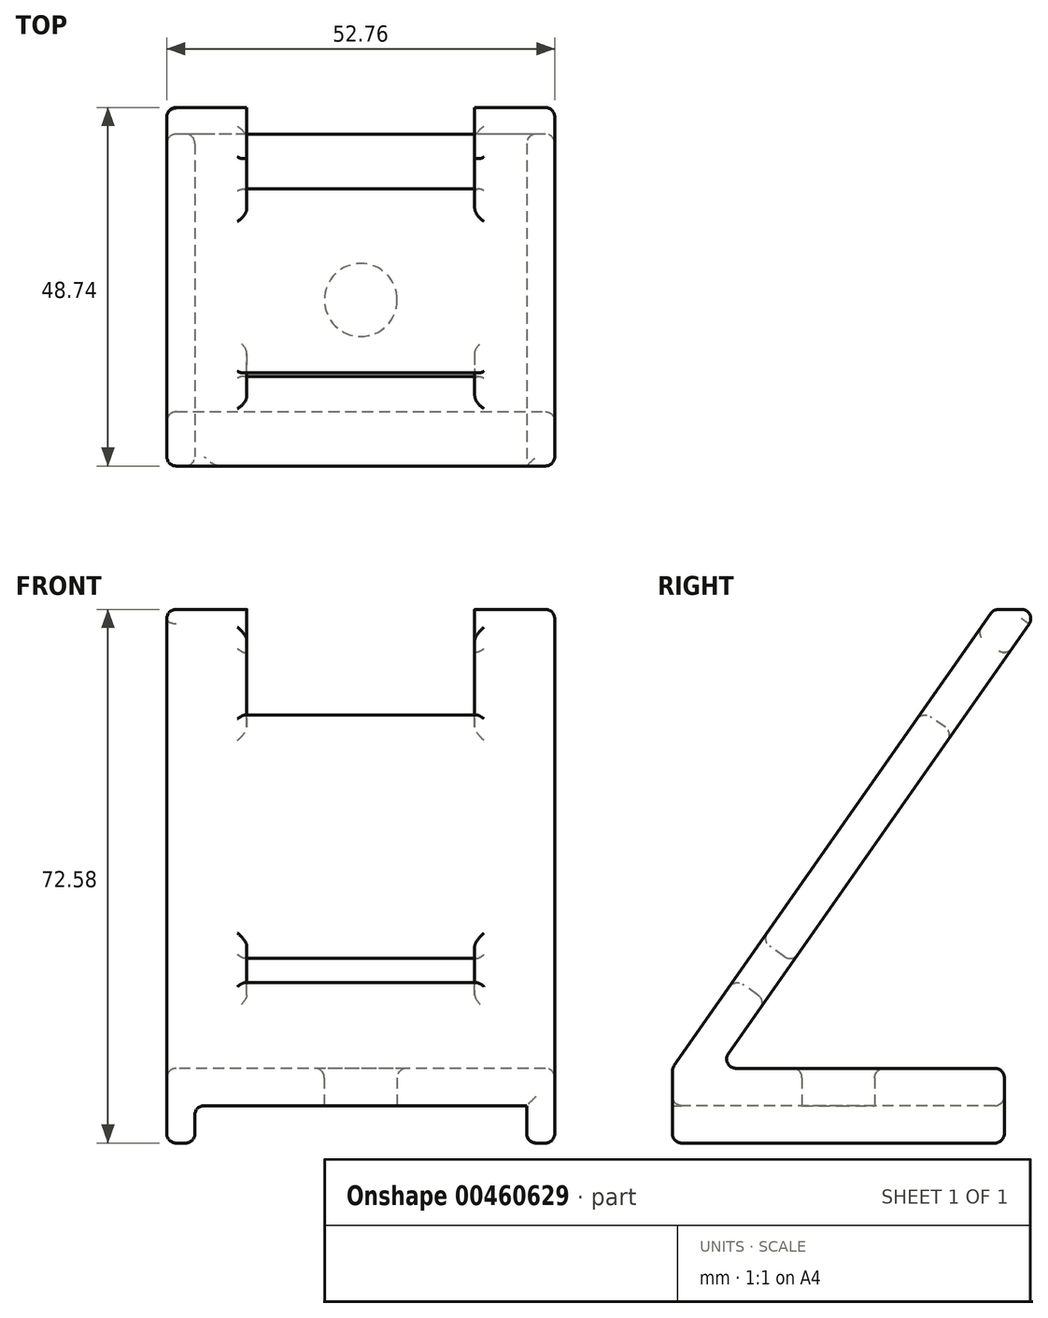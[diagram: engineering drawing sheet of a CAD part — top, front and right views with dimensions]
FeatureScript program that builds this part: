
annotation { "Feature Type Name" : "Feature", "Feature Type Description" : "" }
export const myFeature = defineFeature(function(context is Context, id is Id, definition is map)
    precondition{}
    {
        {
            var Q0;
            Q0=qCreatedBy(makeId("Top.planeOp"),FACE);
            var sketch = newSketch(context, id + "F0", { "sketchPlane" : qUnion([Q0])});
            skLineSegment(sketch, "E0.bottom", {"start": v(26.38, -22.57) * mm, "end": v(-26.38, -22.57) * mm});
            skLineSegment(sketch, "E0.top", {"start": v(26.38, 22.57) * mm, "end": v(-26.38, 22.57) * mm});
            skLineSegment(sketch, "E0.left", {"start": v(26.38, -22.57) * mm, "end": v(26.38, 22.57) * mm});
            skLineSegment(sketch, "E0.right", {"start": v(-26.38, -22.57) * mm, "end": v(-26.38, 22.57) * mm});
            skPoint(sketch, "E0.middle", {"position": v(0, 0) * mm});
            skSolve(sketch);
        }
        {
            var Q0;
            Q0=makeQuery(id+"F0.imprint","IMPRINT",FACE,{"disambiguationData":[TD([[makeQuery(id+"F0.imprint","IMPRINT",EDGE,{"derivedFrom":sQuery(id+"F0.wireOp",EDGE,"E0.bottom")}),-1.0]])]});
            extrude(context, id + "F1", {"entities" : qUnion([Q0]), "depth" : 5.08 * mm});
        }
        {
            var Q0;
            Q0=qCreatedBy(makeId("Top.planeOp"),FACE);
            var sketch = newSketch(context, id + "F2", { "sketchPlane" : qUnion([Q0])});
            skLineSegment(sketch, "E1.0", {"start": v(26.38, -22.57) * mm, "end": v(26.38, 22.57) * mm});
            skLineSegment(sketch, "E2.0", {"start": v(26.38, 22.57) * mm, "end": v(22.57, 22.57) * mm});
            skLineSegment(sketch, "E3.0", {"start": v(-26.38, -22.57) * mm, "end": v(-26.38, 22.57) * mm});
            skLineSegment(sketch, "E4.0", {"start": v(26.38, -22.57) * mm, "end": v(22.57, -22.57) * mm});
            skLineSegment(sketch, "E5", {"start": v(22.57, 22.57) * mm, "end": v(22.57, -22.57) * mm});
            skLineSegment(sketch, "E6", {"start": v(-22.57, 22.57) * mm, "end": v(-22.57, -22.57) * mm});
            skLineSegment(sketch, "E7.trimOffspring", {"start": v(-22.57, 22.57) * mm, "end": v(-26.38, 22.57) * mm});
            skLineSegment(sketch, "E8.trimOffspring", {"start": v(-22.57, -22.57) * mm, "end": v(-26.38, -22.57) * mm});
            skSolve(sketch);
        }
        {
            var Q0;
            Q0=makeQuery(id+"F2.imprint","IMPRINT",FACE,{"disambiguationData":[TD([[makeQuery(id+"F2.imprint","IMPRINT",EDGE,{"derivedFrom":sQuery(id+"F2.wireOp",EDGE,"E1.0")}),1.0]])]});
            var Q1;
            Q1=makeQuery(id+"F2.imprint","IMPRINT",FACE,{"disambiguationData":[TD([[makeQuery(id+"F2.imprint","IMPRINT",EDGE,{"derivedFrom":sQuery(id+"F2.wireOp",EDGE,"E3.0")}),-1.0]])]});
            extrude(context, id + "F3", {"entities" : qUnion([Q0, Q1]), "operationType" : NewBodyOperationType.ADD, "oppositeDirection" : true, "depth" : 5.08 * mm});
        }
        {
            var Q0;
            Q0=qCreatedBy(makeId("Top.planeOp"),FACE);
            var sketch = newSketch(context, id + "F4", { "sketchPlane" : qUnion([Q0])});
            skCircle(sketch, "E9", {"center": v(0, 0) * mm, "radius": 4.95 * mm});
            skSolve(sketch);
        }
        {
            var Q0;
            Q0=makeQuery(id+"F4.imprint","IMPRINT",FACE,{"disambiguationData":[TD([[makeQuery(id+"F4.imprint","IMPRINT",EDGE,{"derivedFrom":sQuery(id+"F4.wireOp",EDGE,"E9")}),1.0]])]});
            extrude(context, id + "F5", {"entities" : qUnion([Q0]), "operationType" : NewBodyOperationType.REMOVE, "depth" : 25.4 * mm});
        }
        {
            var Q0;
            Q0=qCreatedBy(makeId("Right.planeOp"),FACE);
            var sketch = newSketch(context, id + "F6", { "sketchPlane" : qUnion([Q0])});
            skLineSegment(sketch, "E10.0", {"start": v(-22.57, 5.08) * mm, "end": v(22.57, 5.08) * mm});
            skLineSegment(sketch, "E11", {"start": v(-22.57, 5.08) * mm, "end": v(21.14, 67.5) * mm});
            skLineSegment(sketch, "E12", {"start": v(21.14, 67.5) * mm, "end": v(27.34, 67.5) * mm});
            skLineSegment(sketch, "E13", {"start": v(27.34, 67.5) * mm, "end": v(-16.37, 5.08) * mm});
            skSolve(sketch);
        }
        {
            var Q0;
            {var subQ0=sQuery(id+"F6.wireOp",EDGE,"E11");Q0=makeQuery(id+"F6.imprint","IMPRINT",FACE,{"disambiguationData":[TD([[makeQuery(id+"F6.imprint","IMPRINT",EDGE,{"derivedFrom":subQ0}),-1.0]])]});}
            extrude(context, id + "F7", {"entities" : qUnion([Q0]), "operationType" : NewBodyOperationType.ADD, "endBound" : BoundingType.SYMMETRIC, "depth" : 52.76 * mm});
        }
        {
            var Q0;
            Q0=makeQuery(id+"F7.opExtrude","SWEPT_FACE",FACE,{"disambiguationData":[OSD([sQuery(id+"F6.wireOp",EDGE,"E11")])]});
            var sketch = newSketch(context, id + "F8", { "sketchPlane" : qUnion([Q0])});
            skLineSegment(sketch, "E14.bottom", {"start": v(15.5, 50.5) * mm, "end": v(-15.5, 50.5) * mm});
            skLineSegment(sketch, "E14.top", {"start": v(15.5, 63.2) * mm, "end": v(-15.5, 63.2) * mm});
            skLineSegment(sketch, "E14.left", {"start": v(15.5, 50.5) * mm, "end": v(15.5, 63.2) * mm});
            skLineSegment(sketch, "E14.right", {"start": v(-15.5, 50.5) * mm, "end": v(-15.5, 63.2) * mm});
            skPoint(sketch, "E14.middle", {"position": v(0, 56.85) * mm});
            skSolve(sketch);
        }
        {
            var Q0;
            Q0=makeQuery(id+"F8.imprint","IMPRINT",FACE,{"disambiguationData":[TD([[makeQuery(id+"F8.imprint","IMPRINT",EDGE,{"derivedFrom":sQuery(id+"F8.wireOp",EDGE,"E14.bottom")}),-1.0]])]});
            extrude(context, id + "F9", {"entities" : qUnion([Q0]), "operationType" : NewBodyOperationType.REMOVE, "endBound" : BoundingType.THROUGH_ALL, "oppositeDirection" : true, "depth" : 25.4 * mm});
        }
        {
            var Q0;
            Q0=makeQuery(id+"F7.opExtrude","SWEPT_FACE",FACE,{"disambiguationData":[OSD([sQuery(id+"F6.wireOp",EDGE,"E11")])]});
            var sketch = newSketch(context, id + "F10", { "sketchPlane" : qUnion([Q0])});
            skLineSegment(sketch, "E15", {"start": v(15.5, 12.4) * mm, "end": v(15.5, 6.05) * mm});
            skPoint(sketch, "E15.startSnap0", {"position": v(15.5, 56.85) * mm});
            skLineSegment(sketch, "E16", {"start": v(15.5, 6.05) * mm, "end": v(-15.5, 6.05) * mm});
            skLineSegment(sketch, "E17", {"start": v(-15.5, 6.05) * mm, "end": v(-15.5, 12.4) * mm});
            skLineSegment(sketch, "E18", {"start": v(-15.5, 12.4) * mm, "end": v(15.5, 12.4) * mm});
            skSolve(sketch);
        }
        {
            var Q0;
            Q0=makeQuery(id+"F10.imprint","IMPRINT",FACE,{"disambiguationData":[TD([[makeQuery(id+"F10.imprint","IMPRINT",EDGE,{"derivedFrom":sQuery(id+"F10.wireOp",EDGE,"E15")}),-1.0]])]});
            extrude(context, id + "F11", {"entities" : qUnion([Q0]), "operationType" : NewBodyOperationType.REMOVE, "endBound" : BoundingType.UP_TO_NEXT, "oppositeDirection" : true, "depth" : 25.4 * mm});
        }
        {
            var Q0;
            Q0=makeQuery(id+"F7.boolean.opBoolean","MERGE",FACE,{"derivedFrom":[makeQuery(id+"F3.boolean.opBoolean","MERGE",FACE,{"derivedFrom":[makeQuery(id+"F1.opExtrude","SWEPT_FACE",FACE,{"disambiguationData":[OSD([sQuery(id+"F0.wireOp",EDGE,"E0.left")])]}),makeQuery(id+"F3.opExtrude","SWEPT_FACE",FACE,{"disambiguationData":[OSD([sQuery(id+"F2.wireOp",EDGE,"E1.0")])]})]}),makeQuery(id+"F7.opExtrude","CAP_FACE",FACE,{"disambiguationData":[OSD([sQuery(id+"F6.wireOp",EDGE,"E10.0"),sQuery(id+"F6.wireOp",EDGE,"E11"),sQuery(id+"F6.wireOp",EDGE,"E12"),sQuery(id+"F6.wireOp",EDGE,"E13")])],"isStart":false})]});
            var Q1;
            Q1=makeQuery(id+"F7.boolean.opBoolean","MERGE",FACE,{"derivedFrom":[makeQuery(id+"F3.boolean.opBoolean","MERGE",FACE,{"derivedFrom":[makeQuery(id+"F1.opExtrude","SWEPT_FACE",FACE,{"disambiguationData":[OSD([sQuery(id+"F0.wireOp",EDGE,"E0.right")])]}),makeQuery(id+"F3.opExtrude","SWEPT_FACE",FACE,{"disambiguationData":[OSD([sQuery(id+"F2.wireOp",EDGE,"E3.0")])]})]}),makeQuery(id+"F7.opExtrude","CAP_FACE",FACE,{"disambiguationData":[OSD([sQuery(id+"F6.wireOp",EDGE,"E10.0"),sQuery(id+"F6.wireOp",EDGE,"E11"),sQuery(id+"F6.wireOp",EDGE,"E12"),sQuery(id+"F6.wireOp",EDGE,"E13")])],"isStart":true})]});
            var Q2;
            Q2=makeQuery(id+"F7.opExtrude","SWEPT_FACE",FACE,{"disambiguationData":[OSD([sQuery(id+"F6.wireOp",EDGE,"E11")])]});
            var Q3;
            Q3=makeQuery(id+"F7.opExtrude","SWEPT_FACE",FACE,{"disambiguationData":[OSD([sQuery(id+"F6.wireOp",EDGE,"E13")])]});
            var Q4;
            Q4=makeQuery(id+"F1.opExtrude","CAP_FACE",FACE,{"disambiguationData":[OSD([sQuery(id+"F0.wireOp",EDGE,"E0.bottom"),sQuery(id+"F0.wireOp",EDGE,"E0.top"),sQuery(id+"F0.wireOp",EDGE,"E0.left"),sQuery(id+"F0.wireOp",EDGE,"E0.right")])],"isStart":false});
            var Q5;
            Q5=makeQuery(id+"F3.boolean.opBoolean","MERGE",FACE,{"derivedFrom":[makeQuery(id+"F1.opExtrude","SWEPT_FACE",FACE,{"disambiguationData":[OSD([sQuery(id+"F0.wireOp",EDGE,"E0.top")])]}),makeQuery(id+"F3.opExtrude","SWEPT_FACE",FACE,{"disambiguationData":[OSD([sQuery(id+"F2.wireOp",EDGE,"E2.0")])]}),makeQuery(id+"F3.opExtrude","SWEPT_FACE",FACE,{"disambiguationData":[OSD([sQuery(id+"F2.wireOp",EDGE,"E7.trimOffspring")])]})]});
            var Q6;
            Q6=makeQuery(id+"F3.opExtrude","CAP_EDGE",EDGE,{"disambiguationData":[OSD([sQuery(id+"F2.wireOp",EDGE,"E5")])],"isStart":true});
            var Q7;
            Q7=makeQuery(id+"F3.opExtrude","SWEPT_FACE",FACE,{"disambiguationData":[OSD([sQuery(id+"F2.wireOp",EDGE,"E6")])]});
            var Q8;
            Q8=makeQuery(id+"F3.opExtrude","CAP_FACE",FACE,{"disambiguationData":[OSD([sQuery(id+"F2.wireOp",EDGE,"E1.0"),sQuery(id+"F2.wireOp",EDGE,"E2.0"),sQuery(id+"F2.wireOp",EDGE,"E4.0"),sQuery(id+"F2.wireOp",EDGE,"E5")])],"isStart":false});
            var Q9;
            Q9=makeQuery(id+"F3.opExtrude","CAP_FACE",FACE,{"disambiguationData":[OSD([sQuery(id+"F2.wireOp",EDGE,"E3.0"),sQuery(id+"F2.wireOp",EDGE,"E6"),sQuery(id+"F2.wireOp",EDGE,"E7.trimOffspring"),sQuery(id+"F2.wireOp",EDGE,"E8.trimOffspring")])],"isStart":false});
            fillet(context, id + "F12", {"entities" : qUnion([Q0, Q1, Q2, Q3, Q4, Q5, Q6, Q7, Q8, Q9]), "radius" : 1.27 * mm, "tangentPropagation" : true, "allowEdgeOverflow" : false});
        }
        {
            var Q0;
            Q0=makeQuery(id+"F7.opExtrude","SWEPT_FACE",FACE,{"disambiguationData":[OSD([sQuery(id+"F6.wireOp",EDGE,"E11")])]});
            var sketch = newSketch(context, id + "F13", { "sketchPlane" : qUnion([Q0])});
            skLineSegment(sketch, "E19.bottom", {"start": v(-15.5, 56.85) * mm, "end": v(15.5, 56.85) * mm});
            skLineSegment(sketch, "E19.top", {"start": v(-15.5, 74.63) * mm, "end": v(15.5, 74.63) * mm});
            skLineSegment(sketch, "E19.left", {"start": v(-15.5, 63.4) * mm, "end": v(-15.5, 74.63) * mm});
            skLineSegment(sketch, "E19.right", {"start": v(15.5, 56.85) * mm, "end": v(15.5, 74.63) * mm});
            skPoint(sketch, "E20.0.end.orphan", {"position": v(-15.5, 50.5) * mm});
            skPoint(sketch, "E21.0.end.orphan", {"position": v(15.5, 63.2) * mm});
            skPoint(sketch, "E21.0.start.orphan", {"position": v(15.5, 50.5) * mm});
            skLineSegment(sketch, "E22", {"start": v(-15.5, 63.4) * mm, "end": v(-15.5, 56.85) * mm});
            skSolve(sketch);
        }
        {
            var Q0;
            {var subQ0=sQuery(id+"F13.wireOp",EDGE,"E19.top");Q0=makeQuery(id+"F13.imprint","IMPRINT",FACE,{"disambiguationData":[TD([[makeQuery(id+"F13.imprint","IMPRINT",EDGE,{"derivedFrom":subQ0}),-1.0]])]});}
            var Q1;
            {var subQ0=sQuery(id+"F13.wireOp",EDGE,"E19.left");var subQ1=sQuery(id+"F6.wireOp",EDGE,"E11");var subQ2=makeQuery(id+"F7.opExtrude","SWEPT_FACE",FACE,{"disambiguationData":[OSD([subQ1])]});var subQ5=makeQuery(id+"F12.opFillet","BLEND_EDGE",EDGE,{"blendedFrom":[makeQuery(id+"F9.boolean.opBoolean","COPY",EDGE,{"derivedFrom":makeQuery(id+"F9.opExtrude","CAP_EDGE",EDGE,{"disambiguationData":[OSD([sQuery(id+"F8.wireOp",EDGE,"E14.top")])],"isStart":true})}),subQ2],"blendedInto":[subQ2]});var subQ6=makeQuery(id+"F13.imprint","INTERSECT",VERTEX,{"derivedFrom":[subQ5,subQ0]});Q1=makeQuery(id+"F13.imprint","IMPRINT",FACE,{"disambiguationData":[TD([[makeQuery(id+"F13.imprint","IMPRINT",EDGE,{"disambiguationData":[TD([[subQ6,-1.0]])],"derivedFrom":subQ0}),-1.0]])]});}
            var Q2;
            {var subQ6=sQuery(id+"F13.wireOp",EDGE,"E19.bottom");Q2=makeQuery(id+"F13.imprint","IMPRINT",FACE,{"disambiguationData":[TD([[makeQuery(id+"F13.imprint","IMPRINT",EDGE,{"derivedFrom":subQ6}),1.0]])]});}
            extrude(context, id + "F14", {"entities" : qUnion([Q0, Q1, Q2]), "operationType" : NewBodyOperationType.REMOVE, "oppositeDirection" : true, "depth" : 25.4 * mm});
        }
    });
